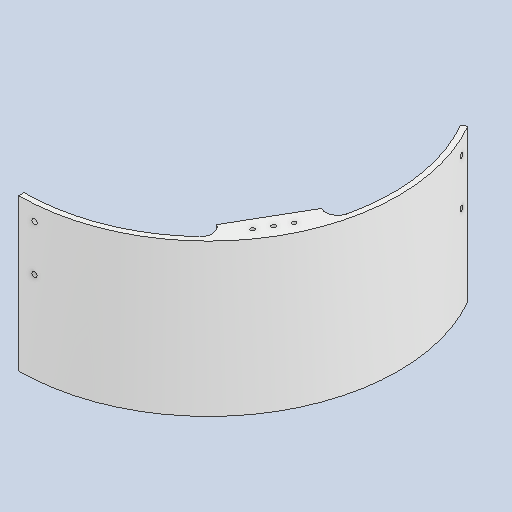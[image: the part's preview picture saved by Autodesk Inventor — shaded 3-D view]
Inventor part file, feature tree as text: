
AUTODESK INVENTOR PART (.ipt)
format: ipt  version: 2023 (Build 270158000, 158)  size: 377,344 bytes
history: native  units: mm
features: sketch x19, extrude x11, hole x8, other x1, fillet x1
ambient origin geometry x8: Origin, YZ Plane, XZ Plane, XY Plane, X Axis, Y Axis, Z Axis, Center Point
bodies: Body1 (feature_tree)
feature tree (40):
  other  "ソリッド1"
  extrude  "押し出し1"  Depth=250.0mm
  extrude  "押し出し2"  Depth=375.0mm TaperAngle=0.0deg
  hole  "穴1"  [1 undecoded]
  hole  "穴2"  [1 undecoded]
  extrude  "押し出し3"  Depth=30.0mm TaperAngle=360.0deg
  extrude  "押し出し4"  Depth=10.0mm
  hole  "穴4"  [1 undecoded]
  hole  "穴5"  [1 undecoded]
  extrude  "押し出し6"  Depth=330.0mm TaperAngle=0.0deg
  extrude  "押し出し7"  Depth=118.0mm
  extrude  "押し出し8"  Depth=30.0mm TaperAngle=360.0deg
  extrude  "押し出し9"  Depth=330.0mm TaperAngle=0.0deg
  extrude  "押し出し11"  Depth=30.0mm
  extrude  "押し出し13"  Depth=30.0mm
  extrude  "押し出し15"  Depth=243.0mm
  fillet  "フィレット1"  Radius=330.0mm
  hole  "穴6"  [1 undecoded]
  hole  "穴7"  [1 undecoded]
  hole  "穴8"  [1 undecoded]
  hole  "穴10"  [1 undecoded]
  sketch  "スケッチ1"
  sketch  "スケッチ2"
  sketch  "スケッチ3"
  sketch  "スケッチ4"
  sketch  "スケッチ5"
  sketch  "スケッチ6"
  sketch  "スケッチ8"
  sketch  "スケッチ11"
  sketch  "スケッチ12"
  sketch  "スケッチ13"
  sketch  "スケッチ14"
  sketch  "スケッチ15"
  sketch  "スケッチ17"
  sketch  "スケッチ19"
  sketch  "スケッチ21"
  sketch  "スケッチ22"
  sketch  "スケッチ23"
  sketch  "スケッチ24"
  sketch  "スケッチ27"
note: 8 required parameter values undecoded (feature->parameter linkage not recoverable at this tier; creation-order binding heuristic only, values carry confidence <= 0.55)
